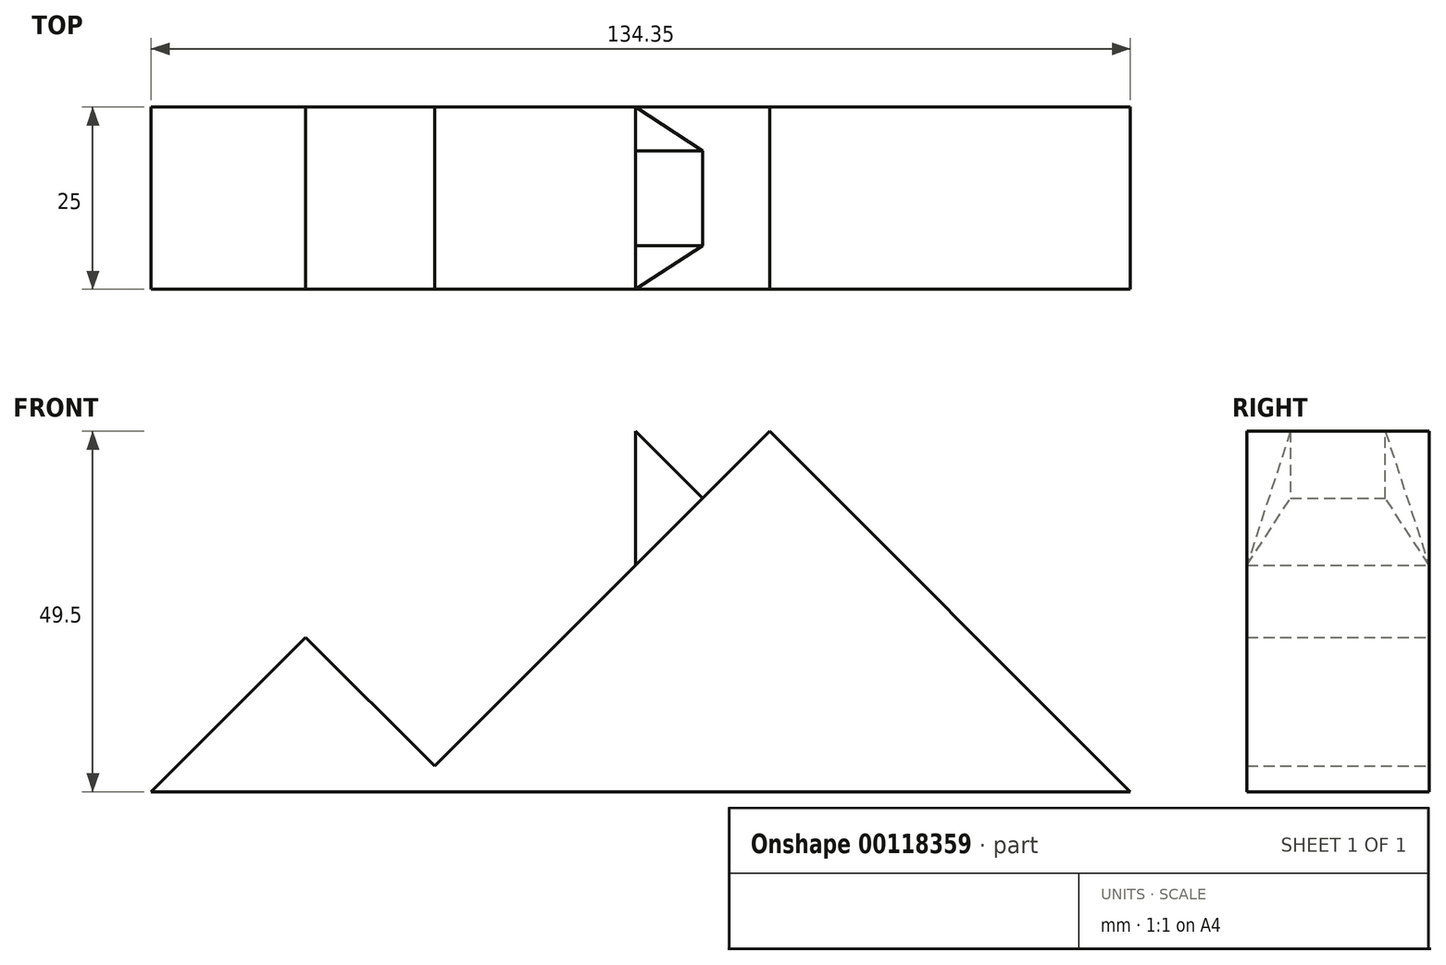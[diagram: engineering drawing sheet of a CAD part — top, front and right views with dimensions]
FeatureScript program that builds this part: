
annotation { "Feature Type Name" : "Feature", "Feature Type Description" : "" }
export const myFeature = defineFeature(function(context is Context, id is Id, definition is map)
    precondition{}
    {
        {
            var Q0;
            Q0=qCreatedBy(makeId("Front.planeOp"),FACE);
            var sketch = newSketch(context, id + "F0", { "sketchPlane" : qUnion([Q0])});
            skLineSegment(sketch, "E0", {"start": v(0, 0) * mm, "end": v(21.21, 21.21) * mm});
            skLineSegment(sketch, "E1", {"start": v(21.21, 21.21) * mm, "end": v(38.9, 3.54) * mm});
            skLineSegment(sketch, "E2", {"start": v(38.9, 3.54) * mm, "end": v(56.57, 21.21) * mm});
            skLineSegment(sketch, "E3", {"start": v(56.57, 21.21) * mm, "end": v(84.85, 49.5) * mm});
            skLineSegment(sketch, "E4", {"start": v(84.85, 49.5) * mm, "end": v(134.35, 0) * mm});
            skLineSegment(sketch, "E5", {"start": v(134.35, 0) * mm, "end": v(0, 0) * mm});
            skLineSegment(sketch, "E6", {"start": v(21.21, 21.21) * mm, "end": v(56.57, 21.21) * mm, "construction": true});
            skLineSegment(sketch, "E7", {"start": v(66.47, 31.11) * mm, "end": v(57.28, 40.3) * mm});
            skLineSegment(sketch, "E8", {"start": v(57.28, 40.3) * mm, "end": v(66.47, 49.5) * mm});
            skLineSegment(sketch, "E9", {"start": v(66.47, 49.5) * mm, "end": v(75.66, 40.3) * mm});
            skLineSegment(sketch, "E10", {"start": v(75.66, 40.3) * mm, "end": v(84.85, 49.5) * mm, "construction": true});
            skSolve(sketch);
        }
        {
            var Q0;
            Q0=makeQuery(id+"F0.imprint","IMPRINT",FACE,{"disambiguationData":[TD([[makeQuery(id+"F0.imprint","IMPRINT",EDGE,{"derivedFrom":sQuery(id+"F0.wireOp",EDGE,"E0")}),-1.0]])]});
            var Q1;
            {var subQ0=sQuery(id+"F0.wireOp",EDGE,"E7");Q1=makeQuery(id+"F0.imprint","IMPRINT",FACE,{"disambiguationData":[TD([[makeQuery(id+"F0.imprint","IMPRINT",EDGE,{"derivedFrom":subQ0}),-1.0]])]});}
            extrude(context, id + "F1", {"entities" : qUnion([Q0, Q1]), "depth" : 25 * mm});
        }
        {
            var Q0;
            Q0=makeQuery(id+"F1.opExtrude","CAP_EDGE",EDGE,{"disambiguationData":[OSD([sQuery(id+"F0.wireOp",EDGE,"E9")])],"isStart":false});
            var Q1;
            Q1=makeQuery(id+"F1.opExtrude","CAP_EDGE",EDGE,{"disambiguationData":[OSD([sQuery(id+"F0.wireOp",EDGE,"E9")])],"isStart":true});
            chamfer(context, id + "F2", {"entities" : qUnion([Q0, Q1]), "chamferType" : ChamferType.TWO_OFFSETS, "width1" : 6 * mm, "oppositeDirection" : false, "width2" : 13 * mm, "tangentPropagation" : true});
        }
        {
            var Q0;
            Q0=makeQuery(id+"F1.opExtrude","SWEPT_EDGE",EDGE,{"disambiguationData":[OSD([sQuery(id+"F0.wireOp",EDGE,"E7"),sQuery(id+"F0.wireOp",EDGE,"E8")])]});
            chamfer(context, id + "F3", {"entities" : qUnion([Q0]), "width" : 13 * mm, "tangentPropagation" : true});
        }
    });
